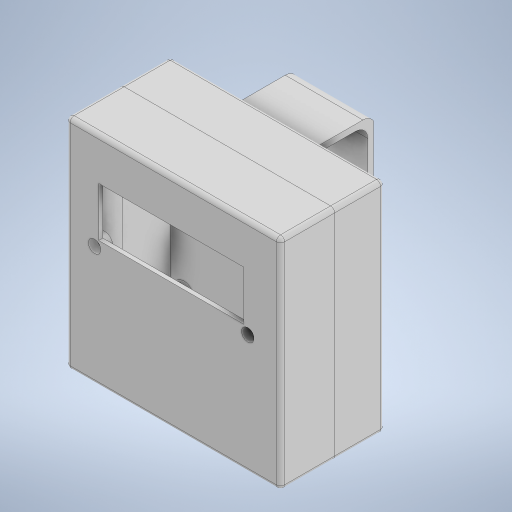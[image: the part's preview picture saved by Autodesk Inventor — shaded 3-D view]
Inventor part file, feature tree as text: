
AUTODESK INVENTOR PART (.ipt)
format: ipt  version: 2023 (Build 270158000, 158)  size: 501,248 bytes
history: native  units: mm
features: other x11, sketch x11, extrude x7, fillet x4, shell x1, split x1
ambient origin geometry x8: Origin, YZ Plane, XZ Plane, XY Plane, X Axis, Y Axis, Z Axis, Center Point
bodies: Body1 (feature_tree), Body2 (feature_tree), Body3 (feature_tree), Body4 (feature_tree)
feature tree (35):
  other  "Sólido1"
  sketch  "Boceto1"  dims[d0=95.0mm d1=95.0mm d2=86.4mm d3=86.7mm]
  extrude  "Extrusión1"  Depth=95.0mm
  fillet  "Empalme2"  Radius=86.4mm
  shell  "Vaciado6"  Thickness=86.7mm
  extrude  "Extrusión2"  Depth=4.8mm
  split  "Dividir1"
  other  "Soporte para fiador1"
  other  "Labio1"
  other  "Labio2"
  extrude  "Extrusión4"  Depth=34.5mm
  other  "Soporte para fiador3"
  other  "Soporte para fiador4"
  extrude  "Extrusión5"  Depth=41.5mm
  fillet  "Empalme4"  Radius=27.5mm
  extrude  "Extrusión9"  Depth=14.0mm
  fillet  "Empalme7"  Radius=10.0mm
  fillet  "Empalme8"  Radius=16.0mm
  extrude  "Extrusión10"  Depth=5.0mm
  extrude  "Extrusión11"  Depth=51.0mm TaperAngle=0.0deg
  sketch  "Boceto2"  dims[d4=4.55mm d5=4.8mm]
  sketch  "Boceto3"  dims[d6=4.8mm d7=34.5mm]
  sketch  "Boceto4"  dims[d8=31.8mm d9=41.5mm d10=27.5mm]
  other  "Sup1"
  sketch  "Boceto6"  dims[d11=9.0mm d12=14.0mm d13=10.0mm d14=16.0mm]
  sketch  "Boceto10"  dims[d15=5.0mm d16=5.0mm]
  sketch  "Boceto12"  dims[d17=5.0mm d18=51.0mm d19=0.0mm]
  sketch  "Boceto13"  dims[d26=2.0mm]
  other  "Sólido4"
  sketch  "Boceto20"  dims[d27=2.0mm]
  sketch  "Boceto21"  dims[d28=71.0mm]
  sketch  "Boceto22"  dims[d29=24.2mm d30=16.0mm d31=20.7mm d32=3.0mm d33=0.0mm d34=132.038888mm d35=25.5mm d36=0.0mm d37=0.0mm d41=75.0mm d42=31.0mm d43=27.5mm d44=73.0mm d45=0.0mm d46=5.0mm d47=5.8mm d48=1.0mm d49=0.0mm d50=5.8mm d51=1.0mm d52=3.0mm d53=0.436332mm d54=0.436332mm d55=0.436332mm d56=0.436332mm d57=90.0deg d58=20.0mm d60=2.0mm d61=2.0mm d62=10.0mm d63=0.0mm d64=1.745329mm d65=0.436332mm d66=0.0mm d67=0.0mm d68=0.0mm d69=360.0deg d70=1.0mm d71=0.9mm d72=0.0mm d73=0.0mm d74=0.0mm d75=0.0mm d76=1.0mm d77=0.9mm d78=0.0mm d79=0.0mm d80=0.0mm d81=0.0mm d82=1.5mm d83=10.8mm d84=5.5mm d85=11.2mm d86=3.0mm d87=0.0mm d113=0.0mm d114=3.5mm d126=20.0mm d128=2.0mm d129=2.0mm d130=2.0mm d131=0.0mm d132=1.745329mm d133=0.436332mm d134=0.0mm d135=0.0mm d136=0.0mm d137=360.0deg d143=5.9mm d144=2.0mm d145=0.0mm d146=5.9mm d147=1.0mm d148=3.0mm d149=0.436332mm d150=0.436332mm d151=0.436332mm d152=0.436332mm d153=90.0deg d154=0.0mm d155=44.0mm d156=5.8mm d157=2.8mm d158=9.5mm d159=0.349066mm d160=0.174533mm d161=20.0mm d163=2.0mm d164=2.0mm d165=2.0mm d166=0.0mm d167=1.745329mm d168=0.436332mm d169=0.0mm d170=0.0mm d171=0.0mm d172=360.0deg d173=38.0mm d174=3.0mm d175=33.5mm d176=5.0mm d177=30.0mm d178=0.0mm d183=6.0mm d203=2.8mm d204=36.0mm d205=0.0mm d206=3.0mm d207=6.0mm d208=0.0mm d209=0.0mm d210=3.0mm d211=0.0mm]
  other  "SuperficieBarrido1"
  other  "Sólido2"
  other  "Sólido3"
